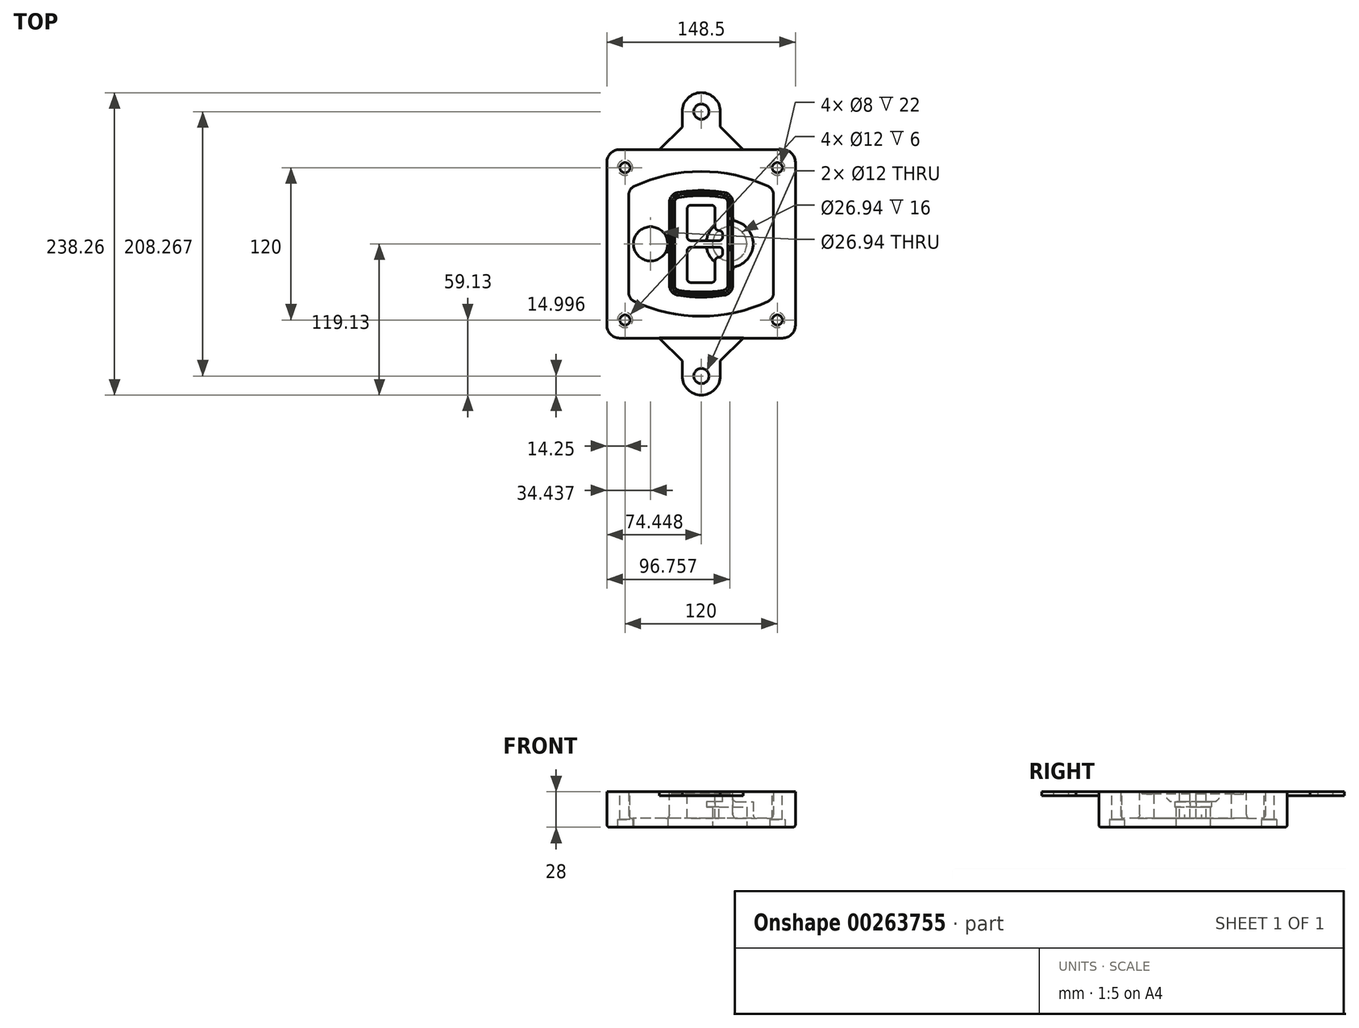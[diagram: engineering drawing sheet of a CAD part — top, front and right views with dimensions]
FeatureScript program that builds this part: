
annotation { "Feature Type Name" : "Feature", "Feature Type Description" : "" }
export const myFeature = defineFeature(function(context is Context, id is Id, definition is map)
    precondition{}
    {
        {
            var Q0;
            Q0=qCreatedBy(makeId("Top.planeOp"),FACE);
            var sketch = newSketch(context, id + "F0", { "sketchPlane" : qUnion([Q0])});
            skPoint(sketch, "E0.rect.middle", {"position": v(0, 0) * mm});
            skLineSegment(sketch, "E1.bottom", {"start": v(-64.25, -74.25) * mm, "end": v(64.25, -74.25) * mm});
            skLineSegment(sketch, "E1.top", {"start": v(-64.25, 74.25) * mm, "end": v(64.25, 74.25) * mm});
            skLineSegment(sketch, "E1.left", {"start": v(-74.25, -64.25) * mm, "end": v(-74.25, 64.25) * mm});
            skLineSegment(sketch, "E1.right", {"start": v(74.25, -64.25) * mm, "end": v(74.25, 64.25) * mm});
            skLineSegment(sketch, "E2", {"start": v(-74.25, 74.25) * mm, "end": v(74.25, -74.25) * mm, "construction": true});
            skLineSegment(sketch, "E3", {"start": v(74.25, 74.25) * mm, "end": v(-74.25, -74.25) * mm, "construction": true});
            skCircle(sketch, "E4", {"center": v(-60, 60) * mm, "radius": 4 * mm});
            skCircle(sketch, "E5", {"center": v(60, 60) * mm, "radius": 4 * mm});
            skCircle(sketch, "E6", {"center": v(60, -60) * mm, "radius": 4 * mm});
            skCircle(sketch, "E7", {"center": v(-60, -60) * mm, "radius": 4 * mm});
            skLineSegment(sketch, "E8", {"start": v(-60, 60) * mm, "end": v(60, 60) * mm, "construction": true});
            skLineSegment(sketch, "E9", {"start": v(60, 60) * mm, "end": v(60, -60) * mm, "construction": true});
            skLineSegment(sketch, "E10", {"start": v(60, -60) * mm, "end": v(-60, -60) * mm, "construction": true});
            skLineSegment(sketch, "E11", {"start": v(-60, -60) * mm, "end": v(-60, 60) * mm, "construction": true});
            skLineSegment(sketch, "E12", {"start": v(-60, 38.83) * mm, "end": v(-60, -38.83) * mm});
            skLineSegment(sketch, "E13", {"start": v(60, 38.83) * mm, "end": v(60, -38.83) * mm});
            skArc(sketch, "E14", {"start": v(54.26, 47.88) * mm, "mid": v(0, 60) * mm, "end": v(-54.26, 47.88) * mm});
            skArc(sketch, "E15", {"start": v(-54.26, -47.88) * mm, "mid": v(0, -60) * mm, "end": v(54.26, -47.88) * mm});
            skLineSegment(sketch, "E16", {"start": v(-60, 0) * mm, "end": v(60, 0) * mm, "construction": true});
            skPoint(sketch, "E17.visualSharp", {"position": v(-60, -45) * mm});
            skArc(sketch, "E17.filletArc", {"start": v(-60, -38.83) * mm, "mid": v(-58.44, -44.2) * mm, "end": v(-54.26, -47.88) * mm});
            skPoint(sketch, "E18.visualSharp", {"position": v(-60, 45) * mm});
            skArc(sketch, "E18.filletArc", {"start": v(-54.26, 47.88) * mm, "mid": v(-58.44, 44.2) * mm, "end": v(-60, 38.83) * mm});
            skPoint(sketch, "E19.visualSharp", {"position": v(60, 45) * mm});
            skArc(sketch, "E19.filletArc", {"start": v(60, 38.83) * mm, "mid": v(58.44, 44.2) * mm, "end": v(54.26, 47.88) * mm});
            skPoint(sketch, "E20.visualSharp", {"position": v(60, -45) * mm});
            skArc(sketch, "E20.filletArc", {"start": v(54.26, -47.88) * mm, "mid": v(58.44, -44.2) * mm, "end": v(60, -38.83) * mm});
            skPoint(sketch, "E21.visualSharp", {"position": v(-74.25, 74.25) * mm});
            skArc(sketch, "E21.filletArc", {"start": v(-64.25, 74.25) * mm, "mid": v(-71.32, 71.32) * mm, "end": v(-74.25, 64.25) * mm});
            skPoint(sketch, "E22.visualSharp", {"position": v(74.25, 74.25) * mm});
            skArc(sketch, "E22.filletArc", {"start": v(74.25, 64.25) * mm, "mid": v(71.32, 71.32) * mm, "end": v(64.25, 74.25) * mm});
            skPoint(sketch, "E23.visualSharp", {"position": v(74.25, -74.25) * mm});
            skArc(sketch, "E23.filletArc", {"start": v(64.25, -74.25) * mm, "mid": v(71.32, -71.32) * mm, "end": v(74.25, -64.25) * mm});
            skPoint(sketch, "E24.visualSharp", {"position": v(-74.25, -74.25) * mm});
            skArc(sketch, "E24.filletArc", {"start": v(-74.25, -64.25) * mm, "mid": v(-71.32, -71.32) * mm, "end": v(-64.25, -74.25) * mm});
            skArc(sketch, "E25.0", {"start": v(57, 38.83) * mm, "mid": v(55.9, 42.58) * mm, "end": v(52.98, 45.17) * mm});
            skLineSegment(sketch, "E25.1", {"start": v(57, 38.83) * mm, "end": v(57, -38.83) * mm});
            skArc(sketch, "E25.2", {"start": v(52.98, -45.17) * mm, "mid": v(55.9, -42.58) * mm, "end": v(57, -38.83) * mm});
            skArc(sketch, "E25.3", {"start": v(-52.98, -45.17) * mm, "mid": v(0, -57) * mm, "end": v(52.98, -45.17) * mm});
            skArc(sketch, "E25.4", {"start": v(-57, -38.83) * mm, "mid": v(-55.9, -42.58) * mm, "end": v(-52.98, -45.17) * mm});
            skArc(sketch, "E25.5", {"start": v(52.98, 45.17) * mm, "mid": v(0, 57) * mm, "end": v(-52.98, 45.17) * mm});
            skLineSegment(sketch, "E25.6", {"start": v(-57, 38.83) * mm, "end": v(-57, -38.83) * mm});
            skArc(sketch, "E25.7", {"start": v(-52.98, 45.17) * mm, "mid": v(-55.9, 42.58) * mm, "end": v(-57, 38.83) * mm});
            skArc(sketch, "E26.0", {"start": v(-55.96, 51.5) * mm, "mid": v(-61.82, 46.33) * mm, "end": v(-64, 38.83) * mm});
            skArc(sketch, "E26.1", {"start": v(55.96, 51.5) * mm, "mid": v(0, 64) * mm, "end": v(-55.96, 51.5) * mm});
            skArc(sketch, "E26.2", {"start": v(64, 38.83) * mm, "mid": v(61.82, 46.33) * mm, "end": v(55.96, 51.5) * mm});
            skLineSegment(sketch, "E26.3", {"start": v(64, 38.83) * mm, "end": v(64, -38.83) * mm});
            skArc(sketch, "E26.4", {"start": v(55.96, -51.5) * mm, "mid": v(61.82, -46.33) * mm, "end": v(64, -38.83) * mm});
            skLineSegment(sketch, "E26.5", {"start": v(-64, 38.83) * mm, "end": v(-64, -38.83) * mm});
            skArc(sketch, "E26.6", {"start": v(-55.96, -51.5) * mm, "mid": v(0, -64) * mm, "end": v(55.96, -51.5) * mm});
            skArc(sketch, "E26.7", {"start": v(-64, -38.83) * mm, "mid": v(-61.82, -46.33) * mm, "end": v(-55.96, -51.5) * mm});
            skSolve(sketch);
        }
        {
            var Q0;
            Q0=makeQuery(id+"F0.imprint","IMPRINT",FACE,{"disambiguationData":[TD([[makeQuery(id+"F0.imprint","IMPRINT",EDGE,{"derivedFrom":sQuery(id+"F0.wireOp",EDGE,"E1.bottom")}),1.0]])]});
            var Q1;
            Q1=makeQuery(id+"F0.imprint","IMPRINT",FACE,{"disambiguationData":[TD([[makeQuery(id+"F0.imprint","IMPRINT",EDGE,{"derivedFrom":sQuery(id+"F0.wireOp",EDGE,"E12")}),1.0]])]});
            var Q2;
            Q2=makeQuery(id+"F0.imprint","IMPRINT",FACE,{"disambiguationData":[TD([[makeQuery(id+"F0.imprint","IMPRINT",EDGE,{"derivedFrom":sQuery(id+"F0.wireOp",EDGE,"E25.0")}),1.0]])]});
            var Q3;
            Q3=makeQuery(id+"F0.imprint","IMPRINT",FACE,{"disambiguationData":[TD([[makeQuery(id+"F0.imprint","IMPRINT",EDGE,{"derivedFrom":sQuery(id+"F0.wireOp",EDGE,"E12")}),-1.0]])]});
            extrude(context, id + "F1", {"entities" : qUnion([Q0, Q1, Q2, Q3]), "oppositeDirection" : true, "depth" : 25 * mm});
        }
        {
            var Q0;
            Q0=makeQuery(id+"F0.imprint","IMPRINT",FACE,{"disambiguationData":[TD([[makeQuery(id+"F0.imprint","IMPRINT",EDGE,{"derivedFrom":sQuery(id+"F0.wireOp",EDGE,"E12")}),1.0]])]});
            extrude(context, id + "F2", {"entities" : qUnion([Q0]), "operationType" : NewBodyOperationType.ADD, "depth" : 3 * mm});
        }
        {
            var Q0;
            Q0=makeQuery(id+"F0.imprint","IMPRINT",FACE,{"disambiguationData":[TD([[makeQuery(id+"F0.imprint","IMPRINT",EDGE,{"derivedFrom":sQuery(id+"F0.wireOp",EDGE,"E25.0")}),1.0]])]});
            extrude(context, id + "F3", {"entities" : qUnion([Q0]), "operationType" : NewBodyOperationType.REMOVE, "oppositeDirection" : true, "depth" : 18 * mm});
        }
        {
            var Q0;
            Q0=makeQuery(id+"F2.opExtrude","CAP_FACE",FACE,{"disambiguationData":[OSD([sQuery(id+"F0.wireOp",EDGE,"E12"),sQuery(id+"F0.wireOp",EDGE,"E13"),sQuery(id+"F0.wireOp",EDGE,"E14"),sQuery(id+"F0.wireOp",EDGE,"E15"),sQuery(id+"F0.wireOp",EDGE,"E17.filletArc"),sQuery(id+"F0.wireOp",EDGE,"E18.filletArc"),sQuery(id+"F0.wireOp",EDGE,"E19.filletArc"),sQuery(id+"F0.wireOp",EDGE,"E20.filletArc"),sQuery(id+"F0.wireOp",EDGE,"E25.0"),sQuery(id+"F0.wireOp",EDGE,"E25.1"),sQuery(id+"F0.wireOp",EDGE,"E25.2"),sQuery(id+"F0.wireOp",EDGE,"E25.3"),sQuery(id+"F0.wireOp",EDGE,"E25.4"),sQuery(id+"F0.wireOp",EDGE,"E25.5"),sQuery(id+"F0.wireOp",EDGE,"E25.6"),sQuery(id+"F0.wireOp",EDGE,"E25.7")])],"isStart":false});
            var sketch = newSketch(context, id + "F4", { "sketchPlane" : qUnion([Q0])});
            skArc(sketch, "E27.0", {"start": v(-18.34, -40.45) * mm, "mid": v(0, -42) * mm, "end": v(18.34, -40.45) * mm});
            skArc(sketch, "E28.0", {"start": v(18.34, 40.45) * mm, "mid": v(0, 42) * mm, "end": v(-18.34, 40.45) * mm});
            skLineSegment(sketch, "E29", {"start": v(-25, 32.57) * mm, "end": v(-25, -32.57) * mm});
            skLineSegment(sketch, "E30", {"start": v(25, 32.57) * mm, "end": v(25, -32.57) * mm});
            skLineSegment(sketch, "E31", {"start": v(-25, 39.1) * mm, "end": v(25, 39.1) * mm, "construction": true});
            skLineSegment(sketch, "E32", {"start": v(-25, -39.1) * mm, "end": v(25, -39.1) * mm, "construction": true});
            skPoint(sketch, "E33.visualSharp", {"position": v(-25, 39.1) * mm});
            skArc(sketch, "E33.filletArc", {"start": v(-18.34, 40.45) * mm, "mid": v(-23.11, 37.73) * mm, "end": v(-25, 32.57) * mm});
            skPoint(sketch, "E34.visualSharp", {"position": v(25, 39.1) * mm});
            skArc(sketch, "E34.filletArc", {"start": v(25, 32.57) * mm, "mid": v(23.11, 37.73) * mm, "end": v(18.34, 40.45) * mm});
            skPoint(sketch, "E35.visualSharp", {"position": v(25, -39.1) * mm});
            skArc(sketch, "E35.filletArc", {"start": v(18.34, -40.45) * mm, "mid": v(23.11, -37.73) * mm, "end": v(25, -32.57) * mm});
            skPoint(sketch, "E36.visualSharp", {"position": v(-25, -39.1) * mm});
            skArc(sketch, "E36.filletArc", {"start": v(-25, -32.57) * mm, "mid": v(-23.11, -37.73) * mm, "end": v(-18.34, -40.45) * mm});
            skArc(sketch, "E37.0", {"start": v(52.98, 45.17) * mm, "mid": v(0, 57) * mm, "end": v(-52.98, 45.17) * mm});
            skArc(sketch, "E37.1", {"start": v(-52.98, 45.17) * mm, "mid": v(-55.9, 42.58) * mm, "end": v(-57, 38.83) * mm});
            skLineSegment(sketch, "E37.2", {"start": v(-57, 38.83) * mm, "end": v(-57, -38.83) * mm});
            skArc(sketch, "E37.3", {"start": v(-57, -38.83) * mm, "mid": v(-55.9, -42.58) * mm, "end": v(-52.98, -45.17) * mm});
            skArc(sketch, "E37.4", {"start": v(-52.98, -45.17) * mm, "mid": v(0, -57) * mm, "end": v(52.98, -45.17) * mm});
            skArc(sketch, "E37.5", {"start": v(52.98, -45.17) * mm, "mid": v(55.9, -42.58) * mm, "end": v(57, -38.83) * mm});
            skLineSegment(sketch, "E37.6", {"start": v(57, 38.83) * mm, "end": v(57, -38.83) * mm});
            skArc(sketch, "E37.7", {"start": v(57, 38.83) * mm, "mid": v(55.9, 42.58) * mm, "end": v(52.98, 45.17) * mm});
            skLineSegment(sketch, "E38.0", {"start": v(23, 32.57) * mm, "end": v(23, -32.57) * mm});
            skArc(sketch, "E38.1", {"start": v(18, -38.48) * mm, "mid": v(21.58, -36.44) * mm, "end": v(23, -32.57) * mm});
            skArc(sketch, "E38.2", {"start": v(-18, -38.48) * mm, "mid": v(0, -40) * mm, "end": v(18, -38.48) * mm});
            skArc(sketch, "E38.3", {"start": v(-23, -32.57) * mm, "mid": v(-21.58, -36.44) * mm, "end": v(-18, -38.48) * mm});
            skLineSegment(sketch, "E38.4", {"start": v(-23, 32.57) * mm, "end": v(-23, -32.57) * mm});
            skArc(sketch, "E38.5", {"start": v(23, 32.57) * mm, "mid": v(21.58, 36.44) * mm, "end": v(18, 38.48) * mm});
            skArc(sketch, "E38.6", {"start": v(-18, 38.48) * mm, "mid": v(-21.58, 36.44) * mm, "end": v(-23, 32.57) * mm});
            skArc(sketch, "E38.7", {"start": v(18, 38.48) * mm, "mid": v(0, 40) * mm, "end": v(-18, 38.48) * mm});
            skArc(sketch, "E39.0", {"start": v(21, 32.57) * mm, "mid": v(20.06, 35.15) * mm, "end": v(17.67, 36.5) * mm});
            skLineSegment(sketch, "E39.1", {"start": v(21, 32.57) * mm, "end": v(21, -32.57) * mm});
            skArc(sketch, "E39.2", {"start": v(17.67, -36.5) * mm, "mid": v(20.06, -35.15) * mm, "end": v(21, -32.57) * mm});
            skArc(sketch, "E39.3", {"start": v(-17.67, -36.5) * mm, "mid": v(0, -38) * mm, "end": v(17.67, -36.5) * mm});
            skArc(sketch, "E39.4", {"start": v(-21, -32.57) * mm, "mid": v(-20.06, -35.15) * mm, "end": v(-17.67, -36.5) * mm});
            skArc(sketch, "E39.5", {"start": v(17.67, 36.5) * mm, "mid": v(0, 38) * mm, "end": v(-17.67, 36.5) * mm});
            skLineSegment(sketch, "E39.6", {"start": v(-21, 32.57) * mm, "end": v(-21, -32.57) * mm});
            skArc(sketch, "E39.7", {"start": v(-17.67, 36.5) * mm, "mid": v(-20.06, 35.15) * mm, "end": v(-21, 32.57) * mm});
            skLineSegment(sketch, "E40", {"start": v(-25, 0) * mm, "end": v(25, 0) * mm, "construction": true});
            skLineSegment(sketch, "E41", {"start": v(-11, 5.5) * mm, "end": v(-11, 27.5) * mm});
            skLineSegment(sketch, "E42", {"start": v(-8, 30.5) * mm, "end": v(8, 30.5) * mm});
            skLineSegment(sketch, "E43", {"start": v(11, 27.5) * mm, "end": v(11, 13.5) * mm});
            skLineSegment(sketch, "E44", {"start": v(14, 10.5) * mm, "end": v(14, 10.5) * mm});
            skLineSegment(sketch, "E45", {"start": v(17, 7.5) * mm, "end": v(17, 5.5) * mm});
            skLineSegment(sketch, "E46", {"start": v(14, 2.5) * mm, "end": v(-8, 2.5) * mm});
            skPoint(sketch, "E47.visualSharp", {"position": v(-11, 30.5) * mm});
            skArc(sketch, "E47.filletArc", {"start": v(-8, 30.5) * mm, "mid": v(-10.12, 29.62) * mm, "end": v(-11, 27.5) * mm});
            skPoint(sketch, "E48.visualSharp", {"position": v(11, 30.5) * mm});
            skArc(sketch, "E48.filletArc", {"start": v(11, 27.5) * mm, "mid": v(10.12, 29.62) * mm, "end": v(8, 30.5) * mm});
            skPoint(sketch, "E49.visualSharp", {"position": v(11, 10.5) * mm});
            skArc(sketch, "E49.filletArc", {"start": v(11, 13.5) * mm, "mid": v(11.88, 11.38) * mm, "end": v(14, 10.5) * mm});
            skPoint(sketch, "E50.visualSharp", {"position": v(17, 10.5) * mm});
            skArc(sketch, "E50.filletArc", {"start": v(17, 7.5) * mm, "mid": v(16.12, 9.62) * mm, "end": v(14, 10.5) * mm});
            skPoint(sketch, "E51.visualSharp", {"position": v(17, 2.5) * mm});
            skArc(sketch, "E51.filletArc", {"start": v(14, 2.5) * mm, "mid": v(16.12, 3.38) * mm, "end": v(17, 5.5) * mm});
            skPoint(sketch, "E52.visualSharp", {"position": v(-11, 2.5) * mm});
            skArc(sketch, "E52.filletArc", {"start": v(-11, 5.5) * mm, "mid": v(-10.12, 3.38) * mm, "end": v(-8, 2.5) * mm});
            skLineSegment(sketch, "E53.0.MirrorCS", {"start": v(14, -2.5) * mm, "end": v(-8, -2.5) * mm});
            skArc(sketch, "E54.0.MirrorCS", {"start": v(-11, -5.5) * mm, "mid": v(-10.12, -3.38) * mm, "end": v(-8, -2.5) * mm});
            skLineSegment(sketch, "E55.0.MirrorCS", {"start": v(-11, -5.5) * mm, "end": v(-11, -27.5) * mm});
            skArc(sketch, "E56.0.MirrorCS", {"start": v(-8, -30.5) * mm, "mid": v(-10.12, -29.62) * mm, "end": v(-11, -27.5) * mm});
            skLineSegment(sketch, "E57.0.MirrorCS", {"start": v(-8, -30.5) * mm, "end": v(8, -30.5) * mm});
            skArc(sketch, "E58.0.MirrorCS", {"start": v(11, -27.5) * mm, "mid": v(10.12, -29.62) * mm, "end": v(8, -30.5) * mm});
            skLineSegment(sketch, "E59.0.MirrorCS", {"start": v(11, -27.5) * mm, "end": v(11, -13.5) * mm});
            skArc(sketch, "E60.0.MirrorCS", {"start": v(11, -13.5) * mm, "mid": v(11.88, -11.38) * mm, "end": v(14, -10.5) * mm});
            skArc(sketch, "E61.0.MirrorCS", {"start": v(17, -7.5) * mm, "mid": v(16.12, -9.62) * mm, "end": v(14, -10.5) * mm});
            skLineSegment(sketch, "E62.0.MirrorCS", {"start": v(17, -7.5) * mm, "end": v(17, -5.5) * mm});
            skArc(sketch, "E63.0.MirrorCS", {"start": v(14, -2.5) * mm, "mid": v(16.12, -3.38) * mm, "end": v(17, -5.5) * mm});
            skSolve(sketch);
        }
        {
            var Q0;
            Q0=makeQuery(id+"F4.imprint","IMPRINT",FACE,{"disambiguationData":[TD([[makeQuery(id+"F4.imprint","IMPRINT",EDGE,{"derivedFrom":sQuery(id+"F4.wireOp",EDGE,"E27.0")}),1.0]])]});
            var Q1;
            Q1=makeQuery(id+"F4.imprint","IMPRINT",FACE,{"disambiguationData":[TD([[makeQuery(id+"F4.imprint","IMPRINT",EDGE,{"derivedFrom":sQuery(id+"F4.wireOp",EDGE,"E38.0")}),-1.0]])]});
            var Q2;
            Q2=makeQuery(id+"F4.imprint","IMPRINT",FACE,{"disambiguationData":[TD([[makeQuery(id+"F4.imprint","IMPRINT",EDGE,{"derivedFrom":sQuery(id+"F4.wireOp",EDGE,"E39.0")}),1.0]])]});
            extrude(context, id + "F5", {"entities" : qUnion([Q0, Q1, Q2]), "operationType" : NewBodyOperationType.ADD, "endBound" : BoundingType.UP_TO_NEXT, "oppositeDirection" : true, "depth" : 25 * mm});
        }
        {
            var Q0;
            Q0=makeQuery(id+"F4.imprint","IMPRINT",FACE,{"disambiguationData":[TD([[makeQuery(id+"F4.imprint","IMPRINT",EDGE,{"derivedFrom":sQuery(id+"F4.wireOp",EDGE,"E38.0")}),-1.0]])]});
            extrude(context, id + "F6", {"entities" : qUnion([Q0]), "operationType" : NewBodyOperationType.REMOVE, "oppositeDirection" : true, "depth" : 2 * mm});
        }
        {
            var Q0;
            Q0=makeQuery(id+"F1.opExtrude","CAP_FACE",FACE,{"disambiguationData":[OSD([sQuery(id+"F0.wireOp",EDGE,"E1.bottom"),sQuery(id+"F0.wireOp",EDGE,"E1.top"),sQuery(id+"F0.wireOp",EDGE,"E1.left"),sQuery(id+"F0.wireOp",EDGE,"E1.right"),sQuery(id+"F0.wireOp",EDGE,"E4"),sQuery(id+"F0.wireOp",EDGE,"E5"),sQuery(id+"F0.wireOp",EDGE,"E6"),sQuery(id+"F0.wireOp",EDGE,"E7"),sQuery(id+"F0.wireOp",EDGE,"E21.filletArc"),sQuery(id+"F0.wireOp",EDGE,"E22.filletArc"),sQuery(id+"F0.wireOp",EDGE,"E23.filletArc"),sQuery(id+"F0.wireOp",EDGE,"E24.filletArc")])],"isStart":false});
            var sketch = newSketch(context, id + "F7", { "sketchPlane" : qUnion([Q0])});
            skCircle(sketch, "E64", {"center": v(22.5, 0) * mm, "radius": 13.47 * mm});
            skCircle(sketch, "E65", {"center": v(-39.81, 0) * mm, "radius": 13.47 * mm});
            skLineSegment(sketch, "E66", {"start": v(74.25, 0) * mm, "end": v(-74.25, 0) * mm});
            skCircle(sketch, "E67", {"center": v(22.5, 0) * mm, "radius": 18.47 * mm});
            skCircle(sketch, "E68", {"center": v(60, -60) * mm, "radius": 6 * mm});
            skCircle(sketch, "E69", {"center": v(-60, -60) * mm, "radius": 6 * mm});
            skCircle(sketch, "E70", {"center": v(-60, 60) * mm, "radius": 6 * mm});
            skCircle(sketch, "E71", {"center": v(60, 60) * mm, "radius": 6 * mm});
            skSolve(sketch);
        }
        {
            var Q0;
            {var subQ1=sQuery(id+"F7.wireOp",EDGE,"E66");var subQ4=sQuery(id+"F7.wireOp",EDGE,"E64");var subQ6=makeQuery(id+"F7.imprint","INTERSECT",VERTEX,{"disambiguationData":[OD(0.0)],"derivedFrom":[subQ4,subQ1]});Q0=makeQuery(id+"F7.imprint","IMPRINT",FACE,{"disambiguationData":[TD([[makeQuery(id+"F7.imprint","IMPRINT",EDGE,{"disambiguationData":[TD([[subQ6,-1.0]])],"derivedFrom":subQ4}),-1.0]])]});}
            var Q1;
            {var subQ0=sQuery(id+"F7.wireOp",EDGE,"E66");var subQ1=sQuery(id+"F7.wireOp",EDGE,"E64");var subQ3=makeQuery(id+"F7.imprint","INTERSECT",VERTEX,{"disambiguationData":[OD(0.0)],"derivedFrom":[subQ1,subQ0]});Q1=makeQuery(id+"F7.imprint","IMPRINT",FACE,{"disambiguationData":[TD([[makeQuery(id+"F7.imprint","IMPRINT",EDGE,{"disambiguationData":[TD([[subQ3,-1.0]])],"derivedFrom":subQ1}),1.0]])]});}
            var Q2;
            {var subQ0=sQuery(id+"F7.wireOp",EDGE,"E66");var subQ1=sQuery(id+"F7.wireOp",EDGE,"E64");var subQ3=makeQuery(id+"F7.imprint","INTERSECT",VERTEX,{"disambiguationData":[OD(0.0)],"derivedFrom":[subQ1,subQ0]});Q2=makeQuery(id+"F7.imprint","IMPRINT",FACE,{"disambiguationData":[TD([[makeQuery(id+"F7.imprint","IMPRINT",EDGE,{"disambiguationData":[TD([[subQ3,1.0]])],"derivedFrom":subQ1}),1.0]])]});}
            var Q3;
            {var subQ1=sQuery(id+"F7.wireOp",EDGE,"E66");var subQ4=sQuery(id+"F7.wireOp",EDGE,"E64");var subQ6=makeQuery(id+"F7.imprint","INTERSECT",VERTEX,{"disambiguationData":[OD(0.0)],"derivedFrom":[subQ4,subQ1]});Q3=makeQuery(id+"F7.imprint","IMPRINT",FACE,{"disambiguationData":[TD([[makeQuery(id+"F7.imprint","IMPRINT",EDGE,{"disambiguationData":[TD([[subQ6,1.0]])],"derivedFrom":subQ4}),-1.0]])]});}
            extrude(context, id + "F8", {"entities" : qUnion([Q0, Q1, Q2, Q3]), "operationType" : NewBodyOperationType.ADD, "oppositeDirection" : true, "depth" : 20 * mm});
        }
        {
            var Q0;
            {var subQ0=sQuery(id+"F7.wireOp",EDGE,"E66");var subQ1=sQuery(id+"F7.wireOp",EDGE,"E64");var subQ3=makeQuery(id+"F7.imprint","INTERSECT",VERTEX,{"disambiguationData":[OD(0.0)],"derivedFrom":[subQ1,subQ0]});Q0=makeQuery(id+"F7.imprint","IMPRINT",FACE,{"disambiguationData":[TD([[makeQuery(id+"F7.imprint","IMPRINT",EDGE,{"disambiguationData":[TD([[subQ3,-1.0]])],"derivedFrom":subQ1}),1.0]])]});}
            var Q1;
            {var subQ0=sQuery(id+"F7.wireOp",EDGE,"E66");var subQ1=sQuery(id+"F7.wireOp",EDGE,"E64");var subQ3=makeQuery(id+"F7.imprint","INTERSECT",VERTEX,{"disambiguationData":[OD(0.0)],"derivedFrom":[subQ1,subQ0]});Q1=makeQuery(id+"F7.imprint","IMPRINT",FACE,{"disambiguationData":[TD([[makeQuery(id+"F7.imprint","IMPRINT",EDGE,{"disambiguationData":[TD([[subQ3,1.0]])],"derivedFrom":subQ1}),1.0]])]});}
            extrude(context, id + "F9", {"entities" : qUnion([Q0, Q1]), "operationType" : NewBodyOperationType.REMOVE, "oppositeDirection" : true, "depth" : 16 * mm});
        }
        {
            var Q0;
            {var subQ0=sQuery(id+"F7.wireOp",EDGE,"E66");var subQ1=sQuery(id+"F7.wireOp",EDGE,"E65");var subQ3=makeQuery(id+"F7.imprint","INTERSECT",VERTEX,{"disambiguationData":[OD(0.0)],"derivedFrom":[subQ1,subQ0]});Q0=makeQuery(id+"F7.imprint","IMPRINT",FACE,{"disambiguationData":[TD([[makeQuery(id+"F7.imprint","IMPRINT",EDGE,{"disambiguationData":[TD([[subQ3,-1.0]])],"derivedFrom":subQ1}),1.0]])]});}
            var Q1;
            {var subQ0=sQuery(id+"F7.wireOp",EDGE,"E66");var subQ1=sQuery(id+"F7.wireOp",EDGE,"E65");var subQ3=makeQuery(id+"F7.imprint","INTERSECT",VERTEX,{"disambiguationData":[OD(0.0)],"derivedFrom":[subQ1,subQ0]});Q1=makeQuery(id+"F7.imprint","IMPRINT",FACE,{"disambiguationData":[TD([[makeQuery(id+"F7.imprint","IMPRINT",EDGE,{"disambiguationData":[TD([[subQ3,1.0]])],"derivedFrom":subQ1}),1.0]])]});}
            extrude(context, id + "F10", {"entities" : qUnion([Q0, Q1]), "operationType" : NewBodyOperationType.REMOVE, "oppositeDirection" : true, "depth" : 25 * mm});
        }
        {
            var Q0;
            Q0=makeQuery(id+"F7.imprint","IMPRINT",FACE,{"disambiguationData":[TD([[makeQuery(id+"F7.imprint","IMPRINT",EDGE,{"derivedFrom":sQuery(id+"F7.wireOp",EDGE,"E68")}),1.0]])]});
            var Q1;
            Q1=makeQuery(id+"F7.imprint","IMPRINT",FACE,{"disambiguationData":[TD([[makeQuery(id+"F7.imprint","IMPRINT",EDGE,{"derivedFrom":makeQuery(id+"F1.opExtrude","CAP_EDGE",EDGE,{"disambiguationData":[OSD([sQuery(id+"F0.wireOp",EDGE,"E5")])],"isStart":false})}),-1.0]])]});
            var Q2;
            Q2=makeQuery(id+"F7.imprint","IMPRINT",FACE,{"disambiguationData":[TD([[makeQuery(id+"F7.imprint","IMPRINT",EDGE,{"derivedFrom":sQuery(id+"F7.wireOp",EDGE,"E69")}),1.0]])]});
            var Q3;
            Q3=makeQuery(id+"F7.imprint","IMPRINT",FACE,{"disambiguationData":[TD([[makeQuery(id+"F7.imprint","IMPRINT",EDGE,{"derivedFrom":makeQuery(id+"F1.opExtrude","CAP_EDGE",EDGE,{"disambiguationData":[OSD([sQuery(id+"F0.wireOp",EDGE,"E4")])],"isStart":false})}),-1.0]])]});
            var Q4;
            Q4=makeQuery(id+"F7.imprint","IMPRINT",FACE,{"disambiguationData":[TD([[makeQuery(id+"F7.imprint","IMPRINT",EDGE,{"derivedFrom":sQuery(id+"F7.wireOp",EDGE,"E70")}),1.0]])]});
            var Q5;
            Q5=makeQuery(id+"F7.imprint","IMPRINT",FACE,{"disambiguationData":[TD([[makeQuery(id+"F7.imprint","IMPRINT",EDGE,{"derivedFrom":makeQuery(id+"F1.opExtrude","CAP_EDGE",EDGE,{"disambiguationData":[OSD([sQuery(id+"F0.wireOp",EDGE,"E7")])],"isStart":false})}),-1.0]])]});
            var Q6;
            Q6=makeQuery(id+"F7.imprint","IMPRINT",FACE,{"disambiguationData":[TD([[makeQuery(id+"F7.imprint","IMPRINT",EDGE,{"derivedFrom":sQuery(id+"F7.wireOp",EDGE,"E71")}),1.0]])]});
            var Q7;
            Q7=makeQuery(id+"F7.imprint","IMPRINT",FACE,{"disambiguationData":[TD([[makeQuery(id+"F7.imprint","IMPRINT",EDGE,{"derivedFrom":makeQuery(id+"F1.opExtrude","CAP_EDGE",EDGE,{"disambiguationData":[OSD([sQuery(id+"F0.wireOp",EDGE,"E6")])],"isStart":false})}),-1.0]])]});
            extrude(context, id + "F11", {"entities" : qUnion([Q0, Q1, Q2, Q3, Q4, Q5, Q6, Q7]), "operationType" : NewBodyOperationType.REMOVE, "oppositeDirection" : true, "depth" : 6 * mm});
        }
        {
            var Q0;
            Q0=makeQuery(id+"F9.boolean.opBoolean","COPY",FACE,{"derivedFrom":makeQuery(id+"F9.opExtrude","CAP_FACE",FACE,{"disambiguationData":[OSD([sQuery(id+"F7.wireOp",EDGE,"E64")])],"isStart":false})});
            var sketch = newSketch(context, id + "F12", { "sketchPlane" : qUnion([Q0])});
            skArc(sketch, "E72.0", {"start": v(11, 14.45) * mm, "mid": v(6.45, 9.13) * mm, "end": v(4.2, 2.5) * mm});
            skArc(sketch, "E72.1", {"start": v(4.2, -2.5) * mm, "mid": v(6.45, -9.13) * mm, "end": v(11, -14.45) * mm});
            skLineSegment(sketch, "E73", {"start": v(4.2, -2.5) * mm, "end": v(14, -2.5) * mm});
            skLineSegment(sketch, "E74.0", {"start": v(14, 2.5) * mm, "end": v(4.2, 2.5) * mm});
            skArc(sketch, "E74.1", {"start": v(14, 2.5) * mm, "mid": v(16.12, 3.38) * mm, "end": v(17, 5.5) * mm});
            skLineSegment(sketch, "E74.2", {"start": v(17, 7.5) * mm, "end": v(17, 5.5) * mm});
            skArc(sketch, "E74.3", {"start": v(17, 7.5) * mm, "mid": v(16.12, 9.62) * mm, "end": v(14, 10.5) * mm});
            skArc(sketch, "E74.4", {"start": v(11, 13.5) * mm, "mid": v(11.88, 11.38) * mm, "end": v(14, 10.5) * mm});
            skLineSegment(sketch, "E74.5", {"start": v(11, 14.45) * mm, "end": v(11, 13.5) * mm});
            skLineSegment(sketch, "E74.7", {"start": v(14, -2.5) * mm, "end": v(4.2, -2.5) * mm});
            skArc(sketch, "E74.8", {"start": v(14, -2.5) * mm, "mid": v(16.12, -3.38) * mm, "end": v(17, -5.5) * mm});
            skLineSegment(sketch, "E74.9", {"start": v(17, -7.5) * mm, "end": v(17, -5.5) * mm});
            skArc(sketch, "E74.10", {"start": v(17, -7.5) * mm, "mid": v(16.12, -9.62) * mm, "end": v(14, -10.5) * mm});
            skArc(sketch, "E74.11", {"start": v(11, -13.5) * mm, "mid": v(11.88, -11.38) * mm, "end": v(14, -10.5) * mm});
            skLineSegment(sketch, "E74.12", {"start": v(11, -14.45) * mm, "end": v(11, -13.5) * mm});
            skPoint(sketch, "E75.orphan", {"position": v(11, -27.5) * mm});
            skPoint(sketch, "E76.orphan", {"position": v(-8, -2.5) * mm});
            skPoint(sketch, "E77.orphan", {"position": v(-8, 2.5) * mm});
            skPoint(sketch, "E78.orphan", {"position": v(11, 27.5) * mm});
            skSolve(sketch);
        }
        {
            var Q0;
            {var subQ7=sQuery(id+"F12.wireOp",EDGE,"E72.0");var subQ14=sQuery(id+"F12.wireOp",EDGE,"E72.1");var subQ16=sQuery(id+"F12.wireOp",EDGE,"E74.1");var subQ18=sQuery(id+"F12.wireOp",EDGE,"E74.8");Q0=qUnion([makeQuery(id+"F12.imprint","IMPRINT",FACE,{"disambiguationData":[TD([[makeQuery(id+"F12.imprint","IMPRINT",EDGE,{"derivedFrom":subQ7}),1.0]])]}),makeQuery(id+"F12.imprint","IMPRINT",FACE,{"disambiguationData":[TD([[makeQuery(id+"F12.imprint","IMPRINT",EDGE,{"derivedFrom":subQ14}),1.0]])]}),makeQuery(id+"F12.imprint","IMPRINT",FACE,{"disambiguationData":[TD([[makeQuery(id+"F12.imprint","IMPRINT",EDGE,{"derivedFrom":subQ16}),1.0]])]}),makeQuery(id+"F12.imprint","IMPRINT",FACE,{"disambiguationData":[TD([[makeQuery(id+"F12.imprint","IMPRINT",EDGE,{"derivedFrom":subQ18}),-1.0]])]})]);}
            var Q1;
            Q1=makeQuery(id+"F5.boolean.opBoolean","SPLIT",FACE,{"disambiguationData":[TD([makeQuery(id+"F5.opExtrude","SWEPT_FACE",FACE,{"disambiguationData":[OSD([sQuery(id+"F4.wireOp",EDGE,"E41")])]})])],"derivedFrom":makeQuery(id+"F3.boolean.opBoolean","COPY",FACE,{"derivedFrom":makeQuery(id+"F3.opExtrude","CAP_FACE",FACE,{"disambiguationData":[OSD([sQuery(id+"F0.wireOp",EDGE,"E25.0"),sQuery(id+"F0.wireOp",EDGE,"E25.1"),sQuery(id+"F0.wireOp",EDGE,"E25.2"),sQuery(id+"F0.wireOp",EDGE,"E25.3"),sQuery(id+"F0.wireOp",EDGE,"E25.4"),sQuery(id+"F0.wireOp",EDGE,"E25.5"),sQuery(id+"F0.wireOp",EDGE,"E25.6"),sQuery(id+"F0.wireOp",EDGE,"E25.7")])],"isStart":false})})});
            extrude(context, id + "F13", {"entities" : qUnion([Q0]), "operationType" : NewBodyOperationType.REMOVE, "endBound" : BoundingType.UP_TO_SURFACE, "endBoundEntityFace" : qUnion([Q1]), "depth" : 25 * mm});
        }
        {
            var Q0;
            Q0=makeQuery(id+"F3.boolean.opBoolean","COPY",EDGE,{"derivedFrom":makeQuery(id+"F3.opExtrude","CAP_EDGE",EDGE,{"disambiguationData":[OSD([sQuery(id+"F0.wireOp",EDGE,"E25.6")])],"isStart":false})});
            var Q1;
            Q1=makeQuery(id+"F8.boolean.opBoolean","INTERSECT",EDGE,{"derivedFrom":[makeQuery(id+"F5.opExtrude","SWEPT_FACE",FACE,{"disambiguationData":[OSD([sQuery(id+"F4.wireOp",EDGE,"E30")])]}),makeQuery(id+"F8.opExtrude","CAP_FACE",FACE,{"disambiguationData":[OSD([sQuery(id+"F7.wireOp",EDGE,"E67")])],"isStart":false})]});
            var Q2;
            Q2=makeQuery(id+"F8.boolean.opBoolean","INTERSECT",EDGE,{"disambiguationData":[OD(1.0)],"derivedFrom":[makeQuery(id+"F5.opExtrude","SWEPT_FACE",FACE,{"disambiguationData":[OSD([sQuery(id+"F4.wireOp",EDGE,"E30")])]}),makeQuery(id+"F8.opExtrude","SWEPT_FACE",FACE,{"disambiguationData":[OSD([sQuery(id+"F7.wireOp",EDGE,"E67")])]})]});
            var Q3;
            {var subQ0=sQuery(id+"F4.wireOp",EDGE,"E30");Q3=makeQuery(id+"F8.boolean.opBoolean","SPLIT",EDGE,{"disambiguationData":[TD([makeQuery(id+"F5.opExtrude","SWEPT_FACE",FACE,{"disambiguationData":[OSD([sQuery(id+"F4.wireOp",EDGE,"E35.filletArc")])]})])],"derivedFrom":makeQuery(id+"F5.opExtrude","CAP_EDGE",EDGE,{"disambiguationData":[OSD([subQ0])],"isStart":false})});}
            var Q4;
            {var subQ0=sQuery(id+"F0.wireOp",EDGE,"E25.7");var subQ1=sQuery(id+"F0.wireOp",EDGE,"E25.1");var subQ2=sQuery(id+"F0.wireOp",EDGE,"E25.6");var subQ3=sQuery(id+"F0.wireOp",EDGE,"E25.5");var subQ4=sQuery(id+"F0.wireOp",EDGE,"E25.4");var subQ5=sQuery(id+"F0.wireOp",EDGE,"E25.0");var subQ6=sQuery(id+"F0.wireOp",EDGE,"E25.2");var subQ7=sQuery(id+"F0.wireOp",EDGE,"E25.3");Q4=makeQuery(id+"F8.boolean.opBoolean","INTERSECT",EDGE,{"derivedFrom":[makeQuery(id+"F5.boolean.opBoolean","SPLIT",FACE,{"disambiguationData":[TD([makeQuery(id+"F2.opExtrude","SWEPT_FACE",FACE,{"disambiguationData":[OSD([subQ5])]})])],"derivedFrom":makeQuery(id+"F3.boolean.opBoolean","COPY",FACE,{"derivedFrom":makeQuery(id+"F3.opExtrude","CAP_FACE",FACE,{"disambiguationData":[OSD([subQ5,subQ1,subQ6,subQ7,subQ4,subQ3,subQ2,subQ0])],"isStart":false})})}),makeQuery(id+"F8.opExtrude","SWEPT_FACE",FACE,{"disambiguationData":[OSD([sQuery(id+"F7.wireOp",EDGE,"E67")])]})]});}
            var Q5;
            Q5=makeQuery(id+"F8.boolean.opBoolean","INTERSECT",EDGE,{"disambiguationData":[OD(0.0)],"derivedFrom":[makeQuery(id+"F5.opExtrude","SWEPT_FACE",FACE,{"disambiguationData":[OSD([sQuery(id+"F4.wireOp",EDGE,"E30")])]}),makeQuery(id+"F8.opExtrude","SWEPT_FACE",FACE,{"disambiguationData":[OSD([sQuery(id+"F7.wireOp",EDGE,"E67")])]})]});
            fillet(context, id + "F14", {"entities" : qUnion([Q0, Q1, Q2, Q3, Q4, Q5]), "radius" : 3 * mm, "tangentPropagation" : true, "allowEdgeOverflow" : false});
        }
        {
            var Q0;
            Q0=makeQuery(id+"F1.opExtrude","CAP_EDGE",EDGE,{"disambiguationData":[OSD([sQuery(id+"F0.wireOp",EDGE,"E1.bottom")])],"isStart":false});
            fillet(context, id + "F15", {"entities" : qUnion([Q0]), "radius" : 2 * mm, "tangentPropagation" : true, "allowEdgeOverflow" : false});
        }
        {
            var Q0;
            {var subQ0=sQuery(id+"F0.wireOp",EDGE,"E22.filletArc");var subQ1=sQuery(id+"F0.wireOp",EDGE,"E7");var subQ2=sQuery(id+"F0.wireOp",EDGE,"E6");var subQ3=sQuery(id+"F0.wireOp",EDGE,"E5");var subQ4=sQuery(id+"F0.wireOp",EDGE,"E4");var subQ5=sQuery(id+"F0.wireOp",EDGE,"E1.bottom");var subQ6=sQuery(id+"F0.wireOp",EDGE,"E21.filletArc");var subQ7=sQuery(id+"F0.wireOp",EDGE,"E1.top");var subQ8=sQuery(id+"F0.wireOp",EDGE,"E1.left");var subQ9=sQuery(id+"F0.wireOp",EDGE,"E1.right");var subQ10=sQuery(id+"F0.wireOp",EDGE,"E23.filletArc");var subQ11=sQuery(id+"F0.wireOp",EDGE,"E24.filletArc");Q0=makeQuery(id+"F2.boolean.opBoolean","SPLIT",FACE,{"disambiguationData":[TD([makeQuery(id+"F1.opExtrude","SWEPT_FACE",FACE,{"disambiguationData":[OSD([subQ5])]})])],"derivedFrom":makeQuery(id+"F1.opExtrude","CAP_FACE",FACE,{"disambiguationData":[OSD([subQ5,subQ7,subQ8,subQ9,subQ4,subQ3,subQ2,subQ1,subQ6,subQ0,subQ10,subQ11])],"isStart":true})});}
            var sketch = newSketch(context, id + "F16", { "sketchPlane" : qUnion([Q0])});
            skSolve(sketch);
        }
        {
            var Q0;
            Q0=makeQuery(id+"F16.imprint","IMPRINT",FACE,{"disambiguationData":[TD([[makeQuery(id+"F16.imprint","IMPRINT",EDGE,{"derivedFrom":makeQuery(id+"F1.opExtrude","CAP_EDGE",EDGE,{"disambiguationData":[OSD([sQuery(id+"F0.wireOp",EDGE,"E1.bottom")])],"isStart":true})}),1.0]])]});
            var sketch = newSketch(context, id + "F17", { "sketchPlane" : qUnion([Q0])});
            skLineSegment(sketch, "E79", {"start": v(-32.9, 74.13) * mm, "end": v(33.3, 74.13) * mm});
            skLineSegment(sketch, "E80", {"start": v(33.3, 74.13) * mm, "end": v(15.1, 92.32) * mm});
            skLineSegment(sketch, "E81", {"start": v(-32.9, 74.13) * mm, "end": v(-14.9, 92.13) * mm});
            skPoint(sketch, "E82.centerSnap0", {"position": v(0.2, 74.13) * mm});
            skCircle(sketch, "E83", {"center": v(0.2, 104.13) * mm, "radius": 6 * mm});
            skLineSegment(sketch, "E84", {"start": v(-14.9, 92.13) * mm, "end": v(-14.9, 104.13) * mm});
            skLineSegment(sketch, "E85", {"start": v(15.1, 92.32) * mm, "end": v(15.1, 104.13) * mm});
            skArc(sketch, "E86", {"start": v(15.1, 104.13) * mm, "mid": v(0.1, 119.13) * mm, "end": v(-14.9, 104.13) * mm});
            skLineSegment(sketch, "E87", {"start": v(-74.45, 0) * mm, "end": v(74.4, 0) * mm, "construction": true});
            skPoint(sketch, "E88.MirrorP", {"position": v(0.2, -74.13) * mm});
            skLineSegment(sketch, "E89.MirrorCS", {"start": v(-32.9, -74.13) * mm, "end": v(33.3, -74.13) * mm});
            skLineSegment(sketch, "E90.MirrorCS", {"start": v(33.3, -74.13) * mm, "end": v(15.1, -92.32) * mm});
            skLineSegment(sketch, "E91.MirrorCS", {"start": v(-32.9, -74.13) * mm, "end": v(-14.9, -92.13) * mm});
            skLineSegment(sketch, "E92.MirrorCS", {"start": v(-14.9, -92.13) * mm, "end": v(-14.9, -104.13) * mm});
            skArc(sketch, "E93.MirrorCS", {"start": v(15.1, -104.13) * mm, "mid": v(0.1, -119.13) * mm, "end": v(-14.9, -104.13) * mm});
            skCircle(sketch, "E94.MirrorC", {"center": v(0.2, -104.13) * mm, "radius": 6 * mm});
            skLineSegment(sketch, "E95.MirrorCS", {"start": v(15.1, -92.32) * mm, "end": v(15.1, -104.13) * mm});
            skSolve(sketch);
        }
        {
            var Q0;
            Q0=makeQuery(id+"F17.imprint","IMPRINT",FACE,{"disambiguationData":[TD([[makeQuery(id+"F17.imprint","IMPRINT",EDGE,{"derivedFrom":sQuery(id+"F17.wireOp",EDGE,"E83")}),-1.0]])]});
            var Q1;
            {var subQ7=sQuery(id+"F17.wireOp",EDGE,"E79");Q1=makeQuery(id+"F17.imprint","IMPRINT",FACE,{"disambiguationData":[TD([[makeQuery(id+"F17.imprint","IMPRINT",EDGE,{"derivedFrom":subQ7}),-1.0]])]});}
            var Q2;
            {var subQ0=sQuery(id+"F17.wireOp",EDGE,"E92.MirrorCS");Q2=makeQuery(id+"F17.imprint","IMPRINT",FACE,{"disambiguationData":[TD([[makeQuery(id+"F17.imprint","IMPRINT",EDGE,{"derivedFrom":subQ0}),1.0]])]});}
            var Q3;
            Q3=makeQuery(id+"F2.opExtrude","CAP_FACE",FACE,{"disambiguationData":[OSD([sQuery(id+"F0.wireOp",EDGE,"E12"),sQuery(id+"F0.wireOp",EDGE,"E13"),sQuery(id+"F0.wireOp",EDGE,"E14"),sQuery(id+"F0.wireOp",EDGE,"E15"),sQuery(id+"F0.wireOp",EDGE,"E17.filletArc"),sQuery(id+"F0.wireOp",EDGE,"E18.filletArc"),sQuery(id+"F0.wireOp",EDGE,"E19.filletArc"),sQuery(id+"F0.wireOp",EDGE,"E20.filletArc"),sQuery(id+"F0.wireOp",EDGE,"E25.0"),sQuery(id+"F0.wireOp",EDGE,"E25.1"),sQuery(id+"F0.wireOp",EDGE,"E25.2"),sQuery(id+"F0.wireOp",EDGE,"E25.3"),sQuery(id+"F0.wireOp",EDGE,"E25.4"),sQuery(id+"F0.wireOp",EDGE,"E25.5"),sQuery(id+"F0.wireOp",EDGE,"E25.6"),sQuery(id+"F0.wireOp",EDGE,"E25.7")])],"isStart":false});
            extrude(context, id + "F18", {"entities" : qUnion([Q0, Q1, Q2]), "operationType" : NewBodyOperationType.ADD, "endBound" : BoundingType.UP_TO_SURFACE, "endBoundEntityFace" : qUnion([Q3]), "depth" : 25 * mm});
        }
    });
